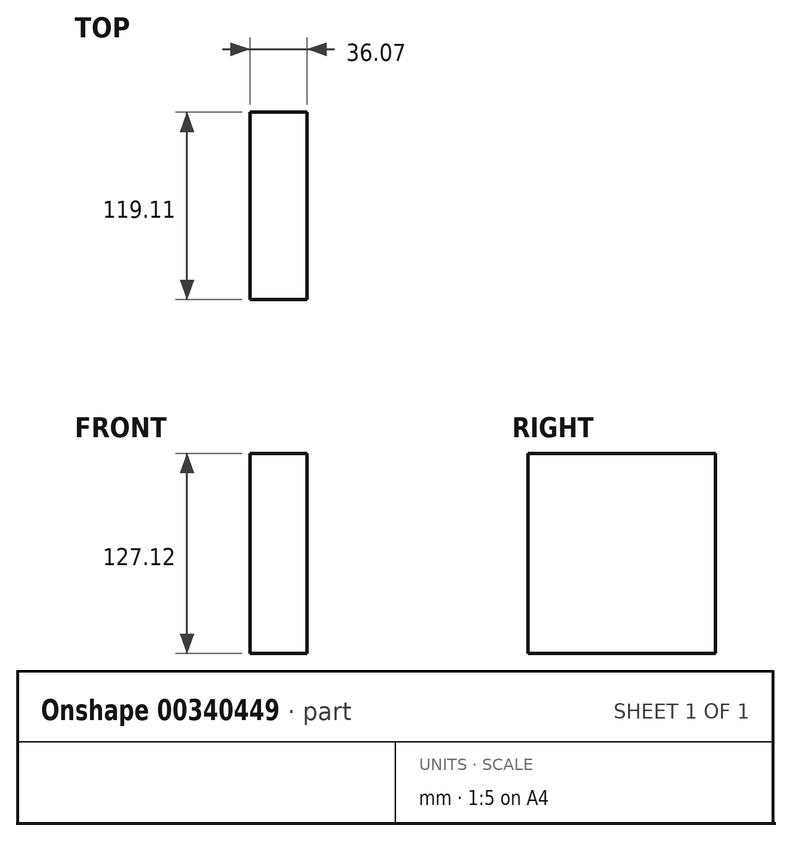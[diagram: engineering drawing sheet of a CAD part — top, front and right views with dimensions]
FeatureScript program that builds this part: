
annotation { "Feature Type Name" : "Feature", "Feature Type Description" : "" }
export const myFeature = defineFeature(function(context is Context, id is Id, definition is map)
    precondition{}
    {
        {
            var Q0;
            Q0=qCreatedBy(makeId("Right.planeOp"),FACE);
            var sketch = newSketch(context, id + "F0", { "sketchPlane" : qUnion([Q0])});
            skLineSegment(sketch, "E0.bottom", {"start": v(-46.29, 64.52) * mm, "end": v(72.82, 64.52) * mm});
            skLineSegment(sketch, "E0.top", {"start": v(-46.29, -62.6) * mm, "end": v(72.82, -62.6) * mm});
            skLineSegment(sketch, "E0.left", {"start": v(-46.29, 64.52) * mm, "end": v(-46.29, -62.6) * mm});
            skLineSegment(sketch, "E0.right", {"start": v(72.82, 64.52) * mm, "end": v(72.82, -62.6) * mm});
            skSolve(sketch);
        }
        {
            var Q0;
            Q0 = qSketchRegion(id + "F0", true);
            extrude(context, id + "F1", {"entities" : qUnion([Q0]), "depth" : 36.07 * mm});
        }
    });
